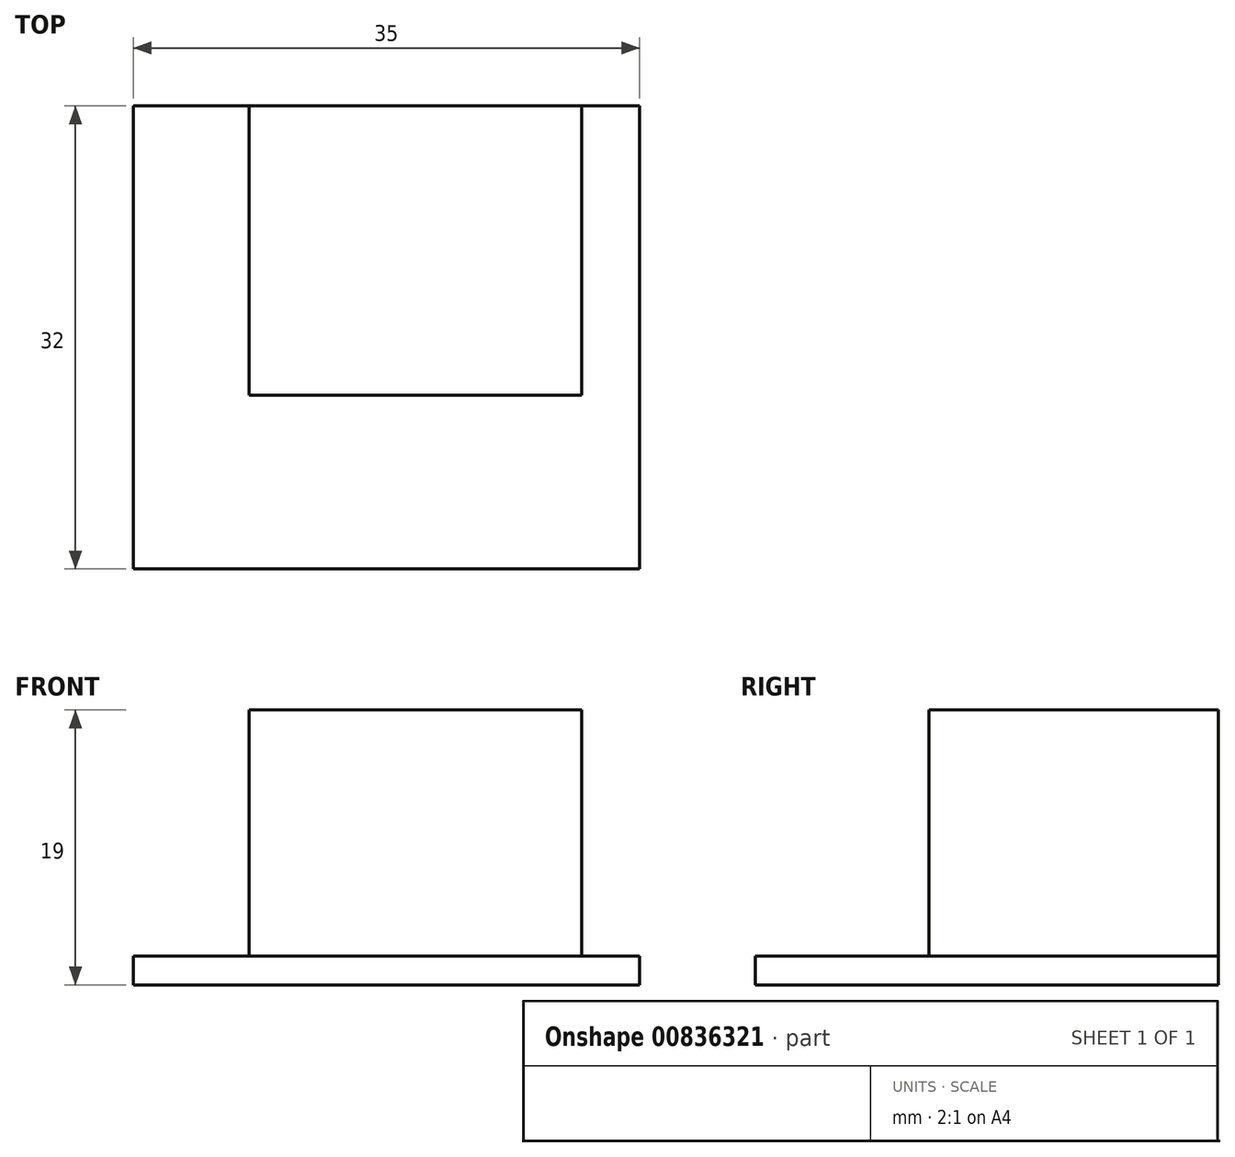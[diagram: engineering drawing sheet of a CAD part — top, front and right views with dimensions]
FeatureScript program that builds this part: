
annotation { "Feature Type Name" : "Feature", "Feature Type Description" : "" }
export const myFeature = defineFeature(function(context is Context, id is Id, definition is map)
    precondition{}
    {
        {
            var Q0;
            Q0=qCreatedBy(makeId("Top.planeOp"),FACE);
            var sketch = newSketch(context, id + "F0", { "sketchPlane" : qUnion([Q0])});
            skLineSegment(sketch, "E0.bottom", {"start": v(17.5, 16) * mm, "end": v(-17.5, 16) * mm});
            skLineSegment(sketch, "E0.top", {"start": v(17.5, -16) * mm, "end": v(-17.5, -16) * mm});
            skLineSegment(sketch, "E0.left", {"start": v(17.5, 16) * mm, "end": v(17.5, -16) * mm});
            skLineSegment(sketch, "E0.right", {"start": v(-17.5, 16) * mm, "end": v(-17.5, -16) * mm});
            skPoint(sketch, "E0.middle", {"position": v(0, 0) * mm});
            skSolve(sketch);
        }
        {
            var Q0;
            Q0=qSketchRegion(id+"F0",true);
            extrude(context, id + "F1", {"entities" : qUnion([Q0]), "depth" : 2 * mm, "offsetDistance" : 25 * mm});
        }
        {
            var Q0;
            Q0=makeQuery(id+"F1.opExtrude","CAP_FACE",FACE,{"disambiguationData":[OSD([sQuery(id+"F0.wireOp",EDGE,"E0.bottom"),sQuery(id+"F0.wireOp",EDGE,"E0.top"),sQuery(id+"F0.wireOp",EDGE,"E0.left"),sQuery(id+"F0.wireOp",EDGE,"E0.right")])],"isStart":false});
            var sketch = newSketch(context, id + "F2", { "sketchPlane" : qUnion([Q0])});
            skLineSegment(sketch, "E1.bottom", {"start": v(-9.5, 16) * mm, "end": v(13.5, 16) * mm});
            skLineSegment(sketch, "E1.top", {"start": v(-9.5, -4) * mm, "end": v(13.5, -4) * mm});
            skLineSegment(sketch, "E1.left", {"start": v(-9.5, 16) * mm, "end": v(-9.5, -4) * mm});
            skLineSegment(sketch, "E1.right", {"start": v(13.5, 16) * mm, "end": v(13.5, -4) * mm});
            skSolve(sketch);
        }
        {
            var Q0;
            Q0=qSketchRegion(id+"F2",true);
            extrude(context, id + "F3", {"entities" : qUnion([Q0]), "operationType" : NewBodyOperationType.ADD, "depth" : 17 * mm, "offsetDistance" : 25 * mm});
        }
    });
